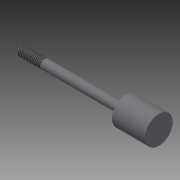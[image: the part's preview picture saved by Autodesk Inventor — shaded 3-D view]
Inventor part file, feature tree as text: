
AUTODESK INVENTOR PART (.ipt)
format: ipt  version: 2014 (Build 180170000, 170)  size: 130,048 bytes
history: native  units: in
note: dims shown in document units (in); Inventor stores cm internally (conversion verified against a paired STEP export)
features: other x49, revolve x3, sketch x3, thread x1
ambient origin geometry x8: Origin, YZ Plane, XZ Plane, XY Plane, X Axis, Y Axis, Z Axis, Center Point
bodies: Solid1 (feature_tree)
feature tree (56):
  revolve  "Revolution1"  [1 undecoded]
  thread  "Thread1"  [1 undecoded]
  revolve  "Revolution2"  [1 undecoded]
  revolve  "Revolution3"  [1 undecoded]
  other  "h1_XY"
  other  "h1_YZ"
  other  "h1_ZX"
  other  "h1_X"
  other  "h1_Y"
  other  "h1_Z"
  other  "h1_Center"
  other  "h2_XY"
  other  "h2_YZ"
  other  "h2_ZX"
  other  "h2_X"
  other  "h2_Y"
  other  "h2_Z"
  other  "h2_Center"
  other  "k1_XY"
  other  "k1_YZ"
  other  "k1_ZX"
  other  "k1_X"
  other  "k1_Y"
  other  "k1_Z"
  other  "k1_Center"
  other  "k2_XY"
  other  "k2_YZ"
  other  "k2_ZX"
  other  "k2_X"
  other  "k2_Y"
  other  "k2_Z"
  other  "k2_Center"
  other  "start_XY"
  other  "start_YZ"
  other  "start_ZX"
  other  "start_X"
  other  "start_Y"
  other  "start_Z"
  other  "start_Center"
  other  "to_prc_XY"
  other  "to_prc_YZ"
  other  "to_prc_ZX"
  other  "to_prc_X"
  other  "to_prc_Y"
  other  "to_prc_Z"
  other  "to_prc_Center"
  other  "to_rod_guide_XY"
  other  "to_rod_guide_YZ"
  other  "to_rod_guide_ZX"
  other  "to_rod_guide_X"
  other  "to_rod_guide_Y"
  other  "to_rod_guide_Z"
  other  "to_rod_guide_Center"
  sketch  "Sketch_3"  dims[d0=360.0deg d1=0.49in d2=2.302in d3=360.0deg]
  sketch  "Sketch_17"
  sketch  "Sketch_12"  dims[d4=360.0deg]
note: 4 required parameter values undecoded (feature->parameter linkage not recoverable at this tier; creation-order binding heuristic only, values carry confidence <= 0.55)